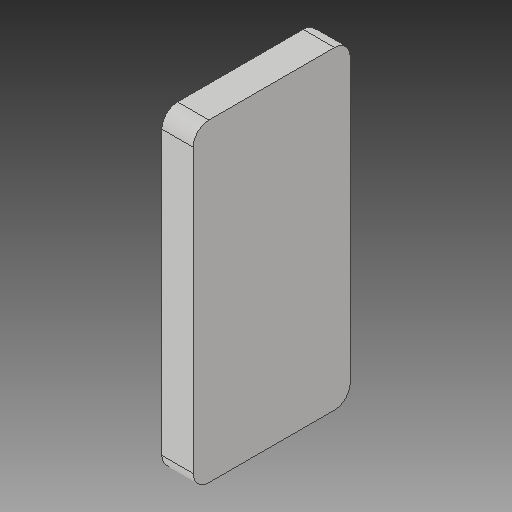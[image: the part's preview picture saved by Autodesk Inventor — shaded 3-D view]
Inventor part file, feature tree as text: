
AUTODESK INVENTOR PART (.ipt)
format: ipt  version: 2017 (Build 210142000, 142)  size: 100,352 bytes
history: native  units: in
note: dims shown in document units (in); Inventor stores cm internally (conversion verified against a paired STEP export)
features: fillet x4, extrude x1, sketch x1
ambient origin geometry x8: Origin, YZ Plane, XZ Plane, XY Plane, X Axis, Y Axis, Z Axis, Center Point
bodies: Solid1 (feature_tree)
feature tree (6):
  extrude  "Extrusion1"  Depth=2.5in
  fillet  "Fillet1"  Radius=0.5in
  fillet  "Fillet2"  Radius=0.25in
  fillet  "Fillet3"  Radius=0.25in
  fillet  "Fillet4"  Radius=0.25in
  sketch  "Sketch1"  dims[d0=5.0in d1=2.5in d2=0.5in d3=0.0in d4=0.25in d5=0.25in d6=0.25in d7=0.25in]
